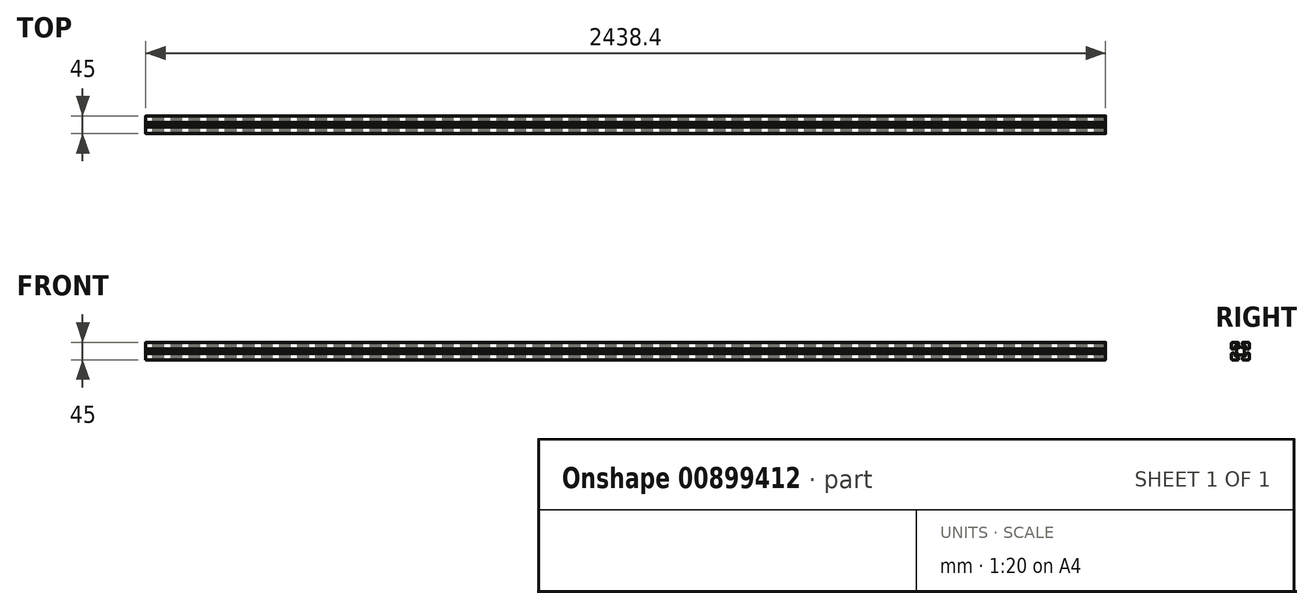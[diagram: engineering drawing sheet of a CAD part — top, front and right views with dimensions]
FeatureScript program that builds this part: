
annotation { "Feature Type Name" : "Feature", "Feature Type Description" : "" }
export const myFeature = defineFeature(function(context is Context, id is Id, definition is map)
    precondition{}
    {
        {
            var Q0;
            Q0=qCreatedBy(makeId("Right.planeOp"),FACE);
            var sketch = newSketch(context, id + "F0", { "sketchPlane" : qUnion([Q0])});
            skLineSegment(sketch, "E0", {"start": v(-20.09, -10.29) * mm, "end": v(-21.29, -10.29) * mm});
            skArc(sketch, "E1", {"start": v(-21.29, -10.29) * mm, "mid": v(-21.5, -10.38) * mm, "end": v(-21.59, -10.59) * mm});
            skLineSegment(sketch, "E2", {"start": v(-21.59, -10.59) * mm, "end": v(-21.59, -23.99) * mm});
            skArc(sketch, "E3", {"start": v(-21.59, -23.99) * mm, "mid": v(-20.7, -26.11) * mm, "end": v(-18.59, -26.99) * mm});
            skLineSegment(sketch, "E4", {"start": v(-18.59, -26.99) * mm, "end": v(-5.19, -26.99) * mm});
            skArc(sketch, "E5", {"start": v(-5.19, -26.99) * mm, "mid": v(-4.98, -26.9) * mm, "end": v(-4.89, -26.69) * mm});
            skLineSegment(sketch, "E6", {"start": v(-4.89, -26.69) * mm, "end": v(-4.89, -25.49) * mm});
            skLineSegment(sketch, "E7", {"start": v(-4.89, -25.49) * mm, "end": v(-4.39, -25.49) * mm});
            skArc(sketch, "E8", {"start": v(-4.39, -25.49) * mm, "mid": v(-4.18, -25.4) * mm, "end": v(-4.09, -25.19) * mm});
            skLineSegment(sketch, "E9", {"start": v(-4.09, -25.19) * mm, "end": v(-4.09, -21.29) * mm});
            skArc(sketch, "E10", {"start": v(-4.09, -21.29) * mm, "mid": v(-4.18, -21.08) * mm, "end": v(-4.39, -20.99) * mm});
            skLineSegment(sketch, "E11", {"start": v(-4.39, -20.99) * mm, "end": v(-9.14, -20.99) * mm});
            skLineSegment(sketch, "E12", {"start": v(-9.14, -20.99) * mm, "end": v(-9.14, -16.88) * mm});
            skLineSegment(sketch, "E13", {"start": v(-9.14, -16.88) * mm, "end": v(-6.25, -13.99) * mm});
            skLineSegment(sketch, "E14", {"start": v(-6.25, -13.99) * mm, "end": v(-2.21, -13.99) * mm});
            skArc(sketch, "E15", {"start": v(-2.21, -13.99) * mm, "mid": v(0.91, -14.49) * mm, "end": v(4.03, -13.99) * mm});
            skLineSegment(sketch, "E16", {"start": v(-20.09, -10.29) * mm, "end": v(-20.09, -9.79) * mm});
            skArc(sketch, "E17", {"start": v(-20.09, -9.79) * mm, "mid": v(-20, -9.58) * mm, "end": v(-19.79, -9.49) * mm});
            skLineSegment(sketch, "E18", {"start": v(-19.79, -9.49) * mm, "end": v(-15.89, -9.49) * mm});
            skArc(sketch, "E19", {"start": v(-15.89, -9.49) * mm, "mid": v(-15.68, -9.58) * mm, "end": v(-15.59, -9.79) * mm});
            skLineSegment(sketch, "E20", {"start": v(-15.59, -9.79) * mm, "end": v(-15.59, -14.54) * mm});
            skLineSegment(sketch, "E21", {"start": v(-15.59, -14.54) * mm, "end": v(-11.48, -14.54) * mm});
            skLineSegment(sketch, "E22", {"start": v(-11.48, -14.54) * mm, "end": v(-8.59, -11.65) * mm});
            skLineSegment(sketch, "E23", {"start": v(-8.59, -11.65) * mm, "end": v(-8.59, -7.61) * mm});
            skLineSegment(sketch, "E24", {"start": v(29.82, -4.49) * mm, "end": v(-31.05, -4.49) * mm});
            skLineSegment(sketch, "E25.MirrorCS", {"start": v(6.71, -25.49) * mm, "end": v(6.21, -25.49) * mm});
            skArc(sketch, "E26.MirrorCS", {"start": v(7.01, -26.99) * mm, "mid": v(6.8, -26.9) * mm, "end": v(6.71, -26.69) * mm});
            skLineSegment(sketch, "E27.MirrorCS", {"start": v(10.41, -11.65) * mm, "end": v(10.41, -7.61) * mm});
            skArc(sketch, "E28.MirrorCS", {"start": v(6.21, -25.49) * mm, "mid": v(6, -25.4) * mm, "end": v(5.91, -25.19) * mm});
            skLineSegment(sketch, "E29.MirrorCS", {"start": v(6.71, -26.69) * mm, "end": v(6.71, -25.49) * mm});
            skArc(sketch, "E30.MirrorCS", {"start": v(5.91, -21.29) * mm, "mid": v(6, -21.08) * mm, "end": v(6.21, -20.99) * mm});
            skLineSegment(sketch, "E31.MirrorCS", {"start": v(10.96, -16.88) * mm, "end": v(8.07, -13.99) * mm});
            skLineSegment(sketch, "E32.MirrorCS", {"start": v(13.3, -14.54) * mm, "end": v(10.41, -11.65) * mm});
            skLineSegment(sketch, "E33.MirrorCS", {"start": v(17.41, -14.54) * mm, "end": v(13.3, -14.54) * mm});
            skLineSegment(sketch, "E34.MirrorCS", {"start": v(17.41, -9.79) * mm, "end": v(17.41, -14.54) * mm});
            skLineSegment(sketch, "E35.MirrorCS", {"start": v(6.21, -20.99) * mm, "end": v(10.96, -20.99) * mm});
            skLineSegment(sketch, "E36.MirrorCS", {"start": v(8.07, -13.99) * mm, "end": v(4.03, -13.99) * mm});
            skArc(sketch, "E37.MirrorCS", {"start": v(4.03, -13.99) * mm, "mid": v(0.91, -14.49) * mm, "end": v(-2.21, -13.99) * mm});
            skLineSegment(sketch, "E38.MirrorCS", {"start": v(10.96, -20.99) * mm, "end": v(10.96, -16.88) * mm});
            skLineSegment(sketch, "E39.MirrorCS", {"start": v(5.91, -25.19) * mm, "end": v(5.91, -21.29) * mm});
            skArc(sketch, "E40.MirrorCS", {"start": v(23.41, -23.99) * mm, "mid": v(22.53, -26.11) * mm, "end": v(20.41, -26.99) * mm});
            skLineSegment(sketch, "E41.MirrorCS", {"start": v(20.41, -26.99) * mm, "end": v(7.01, -26.99) * mm});
            skLineSegment(sketch, "E42.MirrorCS", {"start": v(23.41, -10.59) * mm, "end": v(23.41, -23.99) * mm});
            skArc(sketch, "E43.MirrorCS", {"start": v(17.71, -9.49) * mm, "mid": v(17.5, -9.58) * mm, "end": v(17.41, -9.79) * mm});
            skArc(sketch, "E44.MirrorCS", {"start": v(23.11, -10.29) * mm, "mid": v(23.32, -10.38) * mm, "end": v(23.41, -10.59) * mm});
            skLineSegment(sketch, "E45.MirrorCS", {"start": v(21.91, -10.29) * mm, "end": v(21.91, -9.79) * mm});
            skLineSegment(sketch, "E46.MirrorCS", {"start": v(21.91, -10.29) * mm, "end": v(23.11, -10.29) * mm});
            skArc(sketch, "E47.MirrorCS", {"start": v(21.91, -9.79) * mm, "mid": v(21.82, -9.58) * mm, "end": v(21.61, -9.49) * mm});
            skLineSegment(sketch, "E48.MirrorCS", {"start": v(21.61, -9.49) * mm, "end": v(17.71, -9.49) * mm});
            skLineSegment(sketch, "E49.MirrorCS", {"start": v(6.71, 16.51) * mm, "end": v(6.21, 16.51) * mm});
            skArc(sketch, "E50.MirrorCS", {"start": v(-4.39, 16.51) * mm, "mid": v(-4.18, 16.42) * mm, "end": v(-4.09, 16.21) * mm});
            skLineSegment(sketch, "E51.MirrorCS", {"start": v(-4.89, 16.51) * mm, "end": v(-4.39, 16.51) * mm});
            skArc(sketch, "E52.MirrorCS", {"start": v(5.91, 12.31) * mm, "mid": v(6, 12.1) * mm, "end": v(6.21, 12.01) * mm});
            skLineSegment(sketch, "E53.MirrorCS", {"start": v(6.71, 17.71) * mm, "end": v(6.71, 16.51) * mm});
            skLineSegment(sketch, "E54.MirrorCS", {"start": v(-4.89, 17.71) * mm, "end": v(-4.89, 16.51) * mm});
            skArc(sketch, "E55.MirrorCS", {"start": v(-5.19, 18.01) * mm, "mid": v(-4.98, 17.92) * mm, "end": v(-4.89, 17.71) * mm});
            skArc(sketch, "E56.MirrorCS", {"start": v(-4.09, 12.31) * mm, "mid": v(-4.18, 12.1) * mm, "end": v(-4.39, 12.01) * mm});
            skArc(sketch, "E57.MirrorCS", {"start": v(7.01, 18.01) * mm, "mid": v(6.8, 17.92) * mm, "end": v(6.71, 17.71) * mm});
            skArc(sketch, "E58.MirrorCS", {"start": v(6.21, 16.51) * mm, "mid": v(6, 16.42) * mm, "end": v(5.91, 16.21) * mm});
            skArc(sketch, "E59.MirrorCS", {"start": v(23.11, 1.31) * mm, "mid": v(23.32, 1.4) * mm, "end": v(23.41, 1.61) * mm});
            skLineSegment(sketch, "E60.MirrorCS", {"start": v(21.91, 1.31) * mm, "end": v(21.91, 0.81) * mm});
            skArc(sketch, "E61.MirrorCS", {"start": v(-15.89, 0.51) * mm, "mid": v(-15.68, 0.6) * mm, "end": v(-15.59, 0.81) * mm});
            skArc(sketch, "E62.MirrorCS", {"start": v(-21.29, 1.31) * mm, "mid": v(-21.5, 1.4) * mm, "end": v(-21.59, 1.61) * mm});
            skArc(sketch, "E63.MirrorCS", {"start": v(17.71, 0.51) * mm, "mid": v(17.5, 0.6) * mm, "end": v(17.41, 0.81) * mm});
            skArc(sketch, "E64.MirrorCS", {"start": v(21.91, 0.81) * mm, "mid": v(21.82, 0.6) * mm, "end": v(21.61, 0.51) * mm});
            skLineSegment(sketch, "E65.MirrorCS", {"start": v(21.91, 1.31) * mm, "end": v(23.11, 1.31) * mm});
            skArc(sketch, "E66.MirrorCS", {"start": v(14.31, 5.31) * mm, "mid": v(14.1, 5.4) * mm, "end": v(14.01, 5.61) * mm});
            skArc(sketch, "E67.MirrorCS", {"start": v(-20.09, 0.81) * mm, "mid": v(-20, 0.6) * mm, "end": v(-19.79, 0.51) * mm});
            skLineSegment(sketch, "E68.MirrorCS", {"start": v(-20.09, 1.31) * mm, "end": v(-21.29, 1.31) * mm});
            skLineSegment(sketch, "E69.MirrorCS", {"start": v(-20.09, 1.31) * mm, "end": v(-20.09, 0.81) * mm});
            skLineSegment(sketch, "E70.MirrorCS", {"start": v(8.07, 5.01) * mm, "end": v(4.03, 5.01) * mm});
            skLineSegment(sketch, "E71.MirrorCS", {"start": v(-4.09, 16.21) * mm, "end": v(-4.09, 12.31) * mm});
            skLineSegment(sketch, "E72.MirrorCS", {"start": v(-9.14, 12.01) * mm, "end": v(-9.14, 7.9) * mm});
            skLineSegment(sketch, "E73.MirrorCS", {"start": v(-15.59, 5.56) * mm, "end": v(-11.48, 5.56) * mm});
            skLineSegment(sketch, "E74.MirrorCS", {"start": v(-4.39, 12.01) * mm, "end": v(-9.14, 12.01) * mm});
            skLineSegment(sketch, "E75.MirrorCS", {"start": v(-9.14, 7.9) * mm, "end": v(-6.25, 5.01) * mm});
            skLineSegment(sketch, "E76.MirrorCS", {"start": v(10.96, 12.01) * mm, "end": v(10.96, 7.9) * mm});
            skArc(sketch, "E77.MirrorCS", {"start": v(-21.59, 15.01) * mm, "mid": v(-20.7, 17.13) * mm, "end": v(-18.59, 18.01) * mm});
            skLineSegment(sketch, "E78.MirrorCS", {"start": v(23.41, 1.61) * mm, "end": v(23.41, 15.01) * mm});
            skLineSegment(sketch, "E79.MirrorCS", {"start": v(13.3, 5.56) * mm, "end": v(10.41, 2.67) * mm});
            skLineSegment(sketch, "E80.MirrorCS", {"start": v(-8.59, 2.67) * mm, "end": v(-8.59, -1.37) * mm});
            skLineSegment(sketch, "E81.MirrorCS", {"start": v(-15.59, 0.81) * mm, "end": v(-15.59, 5.56) * mm});
            skLineSegment(sketch, "E82.MirrorCS", {"start": v(10.41, 2.67) * mm, "end": v(10.41, -1.37) * mm});
            skLineSegment(sketch, "E83.MirrorCS", {"start": v(-18.59, 18.01) * mm, "end": v(-5.19, 18.01) * mm});
            skLineSegment(sketch, "E84.MirrorCS", {"start": v(10.96, 7.9) * mm, "end": v(8.07, 5.01) * mm});
            skLineSegment(sketch, "E85.MirrorCS", {"start": v(17.41, 5.56) * mm, "end": v(13.3, 5.56) * mm});
            skArc(sketch, "E86.MirrorCS", {"start": v(23.41, 15.01) * mm, "mid": v(22.53, 17.13) * mm, "end": v(20.41, 18.01) * mm});
            skLineSegment(sketch, "E87.MirrorCS", {"start": v(5.91, 16.21) * mm, "end": v(5.91, 12.31) * mm});
            skLineSegment(sketch, "E88.MirrorCS", {"start": v(17.41, 0.81) * mm, "end": v(17.41, 5.56) * mm});
            skLineSegment(sketch, "E89.MirrorCS", {"start": v(-11.48, 5.56) * mm, "end": v(-8.59, 2.67) * mm});
            skLineSegment(sketch, "E90.MirrorCS", {"start": v(-6.25, 5.01) * mm, "end": v(-2.21, 5.01) * mm});
            skLineSegment(sketch, "E91.MirrorCS", {"start": v(-21.59, 1.61) * mm, "end": v(-21.59, 15.01) * mm});
            skArc(sketch, "E92.MirrorCS", {"start": v(4.03, 5.01) * mm, "mid": v(0.91, 5.51) * mm, "end": v(-2.21, 5.01) * mm});
            skLineSegment(sketch, "E93.MirrorCS", {"start": v(6.21, 12.01) * mm, "end": v(10.96, 12.01) * mm});
            skArc(sketch, "E94.MirrorCS", {"start": v(-2.21, 5.01) * mm, "mid": v(0.91, 5.51) * mm, "end": v(4.03, 5.01) * mm});
            skLineSegment(sketch, "E95.MirrorCS", {"start": v(20.41, 18.01) * mm, "end": v(7.01, 18.01) * mm});
            skLineSegment(sketch, "E96.MirrorCS", {"start": v(-19.79, 0.51) * mm, "end": v(-15.89, 0.51) * mm});
            skLineSegment(sketch, "E97.MirrorCS", {"start": v(21.61, 0.51) * mm, "end": v(17.71, 0.51) * mm});
            skLineSegment(sketch, "E98.MirrorCS", {"start": v(0.91, -27.65) * mm, "end": v(0.91, 19.82) * mm});
            skArc(sketch, "E99", {"start": v(-8.59, -1.37) * mm, "mid": v(-9.09, -4.49) * mm, "end": v(-8.59, -7.61) * mm});
            skArc(sketch, "E100", {"start": v(10.41, -7.61) * mm, "mid": v(10.91, -4.49) * mm, "end": v(10.41, -1.37) * mm});
            skSolve(sketch);
        }
        {
            var Q0;
            Q0=qSketchRegion(id+"F0",true);
            extrude(context, id + "F1", {"entities" : qUnion([Q0]), "depth" : 2438.4 * mm, "offsetDistance" : 25.4 * mm});
        }
    });
